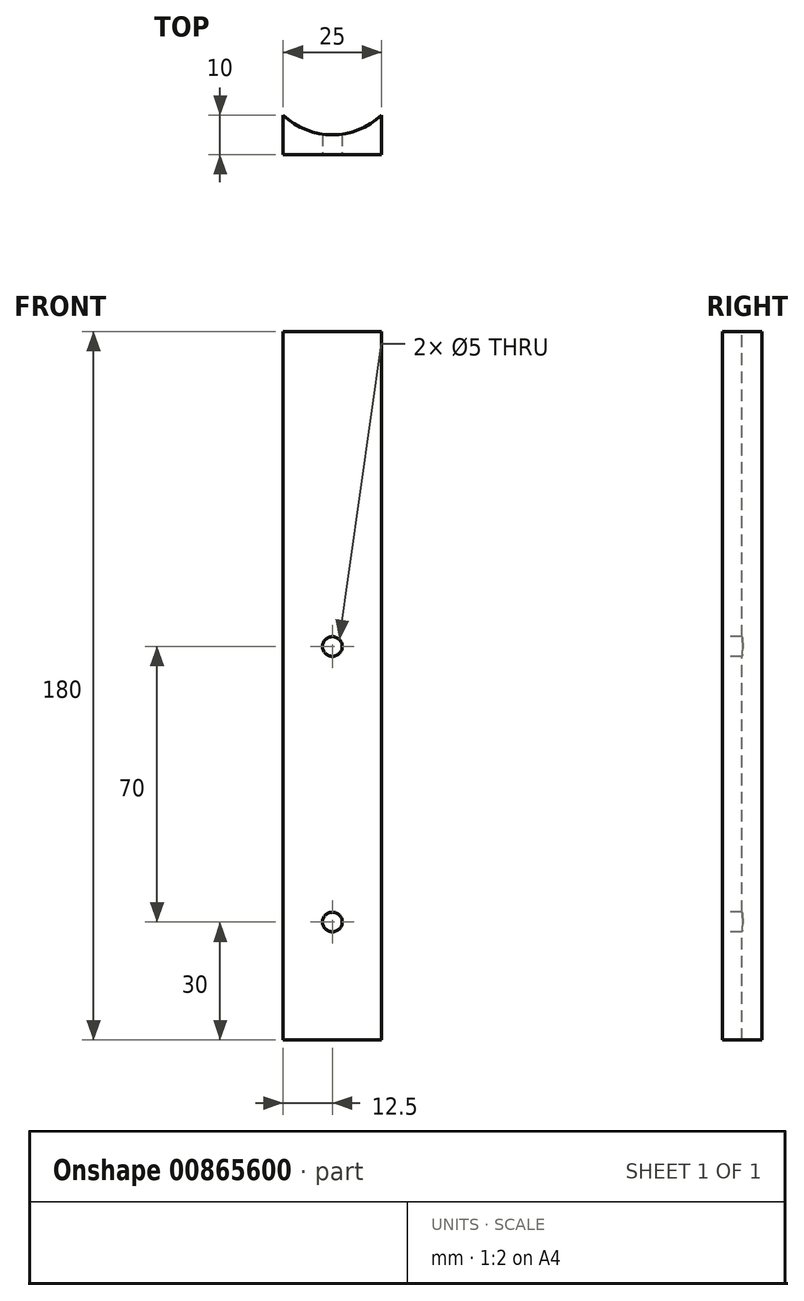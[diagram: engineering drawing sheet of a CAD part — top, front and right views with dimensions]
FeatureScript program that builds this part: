
annotation { "Feature Type Name" : "Feature", "Feature Type Description" : "" }
export const myFeature = defineFeature(function(context is Context, id is Id, definition is map)
    precondition{}
    {
        {
            var Q0;
            Q0=qCreatedBy(makeId("Front.planeOp"),FACE);
            var sketch = newSketch(context, id + "F0", { "sketchPlane" : qUnion([Q0])});
            skLineSegment(sketch, "E0.bottom", {"start": v(-5, 90) * mm, "end": v(5, 90) * mm});
            skLineSegment(sketch, "E0.top", {"start": v(-5, -90) * mm, "end": v(5, -90) * mm});
            skLineSegment(sketch, "E0.left", {"start": v(-5, 90) * mm, "end": v(-5, -90) * mm});
            skLineSegment(sketch, "E0.right", {"start": v(5, 90) * mm, "end": v(5, -90) * mm});
            skPoint(sketch, "E1", {"position": v(0, 0) * mm});
            skPoint(sketch, "E1.positionSnap0", {"position": v(5, 0) * mm});
            skPoint(sketch, "E1.positionSnap1", {"position": v(0, 90) * mm});
            skPoint(sketch, "E2", {"position": v(-5, 90) * mm});
            skSolve(sketch);
        }
        {
            var Q0;
            Q0 = qSketchRegion(id + "F0", true);
            extrude(context, id + "F1", {"entities" : qUnion([Q0]), "endBound" : BoundingType.SYMMETRIC, "depth" : 25 * mm, "offsetDistance" : 25 * mm});
        }
        {
            var Q0;
            Q0=makeQuery(id+"F1.opExtrude","SWEPT_FACE",FACE,{"disambiguationData":[OSD([sQuery(id+"F0.wireOp",EDGE,"E0.bottom")])]});
            var sketch = newSketch(context, id + "F2", { "sketchPlane" : qUnion([Q0])});
            skArc(sketch, "E3", {"start": v(-5, -12.5) * mm, "mid": v(0, 0) * mm, "end": v(-5, 12.5) * mm});
            skSolve(sketch);
        }
        {
            var Q0;
            Q0=makeQuery(id+"F2.imprint","IMPRINT",FACE,{"disambiguationData":[TD([[makeQuery(id+"F2.imprint","IMPRINT",EDGE,{"derivedFrom":sQuery(id+"F2.wireOp",EDGE,"E3")}),1.0]])]});
            extrude(context, id + "F3", {"entities" : qUnion([Q0]), "operationType" : NewBodyOperationType.REMOVE, "endBound" : BoundingType.THROUGH_ALL, "oppositeDirection" : true, "depth" : 25 * mm, "offsetDistance" : 25 * mm});
        }
        {
            var Q0;
            Q0=qCreatedBy(makeId("Front.planeOp"),FACE);
            var sketch = newSketch(context, id + "F4", { "sketchPlane" : qUnion([Q0])});
            skLineSegment(sketch, "E4", {"start": v(0, 56.32) * mm, "end": v(0, 0) * mm, "construction": true});
            skLineSegment(sketch, "E5", {"start": v(0, 0) * mm, "end": v(0, -64.38) * mm, "construction": true});
            skSolve(sketch);
        }
        {
            var Q0;
            Q0=makeQuery(id+"F1.opExtrude","SWEPT_BODY",BODY,{"disambiguationData":[OSD([sQuery(id+"F0.wireOp",EDGE,"E0.bottom"),sQuery(id+"F0.wireOp",EDGE,"E0.top"),sQuery(id+"F0.wireOp",EDGE,"E0.left"),sQuery(id+"F0.wireOp",EDGE,"E0.right")])]});
            var Q1;
            Q1=sQuery(id+"F4.wireOp",EDGE,"E4");
            transform(context, id + "F5", {"entities" : qUnion([Q0]), "transformType" : TransformType.ROTATION, "transformAxis" : qUnion([Q1]), "angle" : 90 * degree, "makeCopy" : false});
        }
        {
            var Q0;
            Q0=makeQuery(id+"F1.opExtrude","SWEPT_FACE",FACE,{"disambiguationData":[OSD([sQuery(id+"F0.wireOp",EDGE,"E0.right")])]});
            var sketch = newSketch(context, id + "F6", { "sketchPlane" : qUnion([Q0])});
            skCircle(sketch, "E6", {"center": v(0, -60) * mm, "radius": 2.5 * mm});
            skCircle(sketch, "E7", {"center": v(0, 10) * mm, "radius": 2.5 * mm});
            skSolve(sketch);
        }
        {
            var Q0;
            Q0=makeQuery(id+"F6.imprint","IMPRINT",FACE,{"disambiguationData":[TD([[makeQuery(id+"F6.imprint","IMPRINT",EDGE,{"derivedFrom":sQuery(id+"F6.wireOp",EDGE,"E7")}),1.0]])]});
            var Q1;
            Q1=makeQuery(id+"F6.imprint","IMPRINT",FACE,{"disambiguationData":[TD([[makeQuery(id+"F6.imprint","IMPRINT",EDGE,{"derivedFrom":sQuery(id+"F6.wireOp",EDGE,"E6")}),1.0]])]});
            extrude(context, id + "F7", {"entities" : qUnion([Q0, Q1]), "operationType" : NewBodyOperationType.REMOVE, "endBound" : BoundingType.THROUGH_ALL, "oppositeDirection" : true, "depth" : 25 * mm, "offsetDistance" : 25 * mm});
        }
    });
